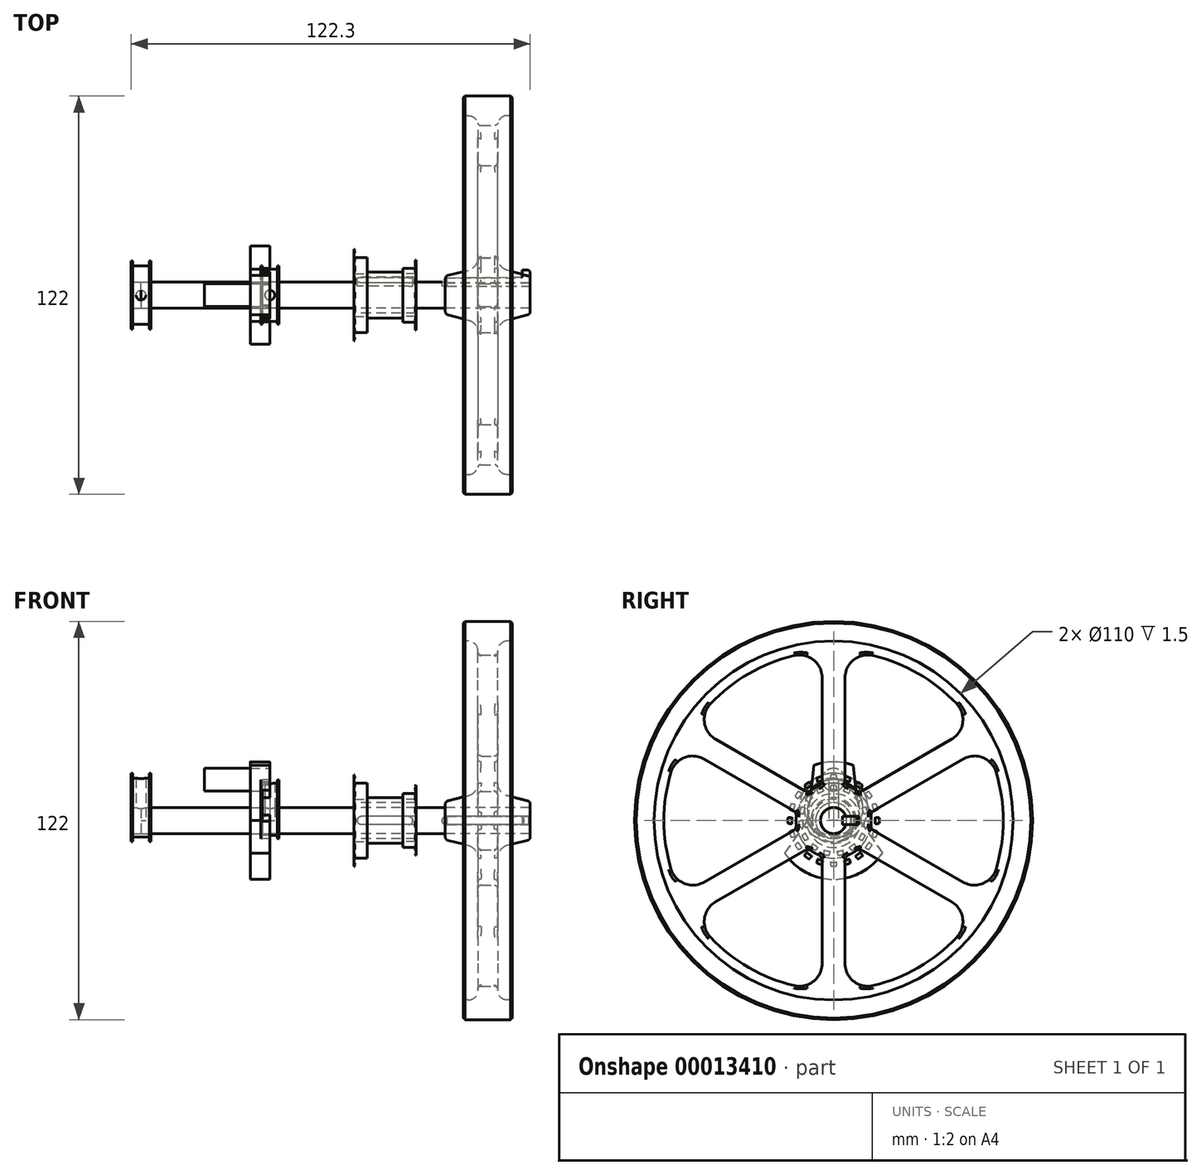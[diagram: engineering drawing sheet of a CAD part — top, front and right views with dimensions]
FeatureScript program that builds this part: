
annotation { "Feature Type Name" : "Feature", "Feature Type Description" : "" }
export const myFeature = defineFeature(function(context is Context, id is Id, definition is map)
    precondition{}
    {
        {
            var Q0;
            Q0=qCreatedBy(makeId("Right.planeOp"),FACE);
            var sketch = newSketch(context, id + "F0", { "sketchPlane" : qUnion([Q0])});
            skCircle(sketch, "E0", {"center": v(0, 0) * mm, "radius": 4 * mm});
            skSolve(sketch);
        }
        {
            var Q0;
            Q0=makeQuery(id+"F0.imprint","IMPRINT",FACE,{"disambiguationData":[TD([[makeQuery(id+"F0.imprint","IMPRINT",EDGE,{"derivedFrom":sQuery(id+"F0.wireOp",EDGE,"E0")}),1.0]])]});
            extrude(context, id + "F1", {"entities" : qUnion([Q0]), "oppositeDirection" : true, "depth" : 39.5 * mm});
        }
        {
            var Q0;
            Q0=makeQuery(id+"F1.opExtrude","CAP_FACE",FACE,{"disambiguationData":[OSD([sQuery(id+"F0.wireOp",EDGE,"E0")])],"isStart":true});
            var sketch = newSketch(context, id + "F2", { "sketchPlane" : qUnion([Q0])});
            skCircle(sketch, "E1", {"center": v(0, 0) * mm, "radius": 18 * mm});
            skLineSegment(sketch, "E2", {"start": v(0, 0) * mm, "end": v(0, 12.5) * mm, "construction": true});
            skCircle(sketch, "E3", {"center": v(0, 12.5) * mm, "radius": 3.5 * mm});
            skLineSegment(sketch, "E4.0", {"start": v(6, 0) * mm, "end": v(6, 16.97) * mm, "construction": true});
            skLineSegment(sketch, "E5", {"start": v(0, 0) * mm, "end": v(8, 0) * mm, "construction": true});
            skLineSegment(sketch, "E6", {"start": v(0, 0) * mm, "end": v(15, 0) * mm, "construction": true});
            skLineSegment(sketch, "E7", {"start": v(15, 0) * mm, "end": v(15, -9.95) * mm, "construction": true});
            skLineSegment(sketch, "E8", {"start": v(6, 16.97) * mm, "end": v(8, 0) * mm});
            skLineSegment(sketch, "E9", {"start": v(8, 0) * mm, "end": v(15, -9.95) * mm});
            skLineSegment(sketch, "E10.0.MirrorCS", {"start": v(-6, 16.97) * mm, "end": v(-8, 0) * mm});
            skLineSegment(sketch, "E11.0.MirrorCS", {"start": v(-8, 0) * mm, "end": v(-15, -9.95) * mm});
            skSolve(sketch);
        }
        {
            var Q0;
            Q0=makeQuery(id+"F2.imprint","IMPRINT",FACE,{"disambiguationData":[TD([[makeQuery(id+"F2.imprint","IMPRINT",EDGE,{"derivedFrom":sQuery(id+"F2.wireOp",EDGE,"E3")}),-1.0]])]});
            extrude(context, id + "F3", {"entities" : qUnion([Q0]), "oppositeDirection" : true, "depth" : 6 * mm});
        }
        {
            var Q0;
            Q0=makeQuery(id+"F2.imprint","IMPRINT",FACE,{"disambiguationData":[TD([[makeQuery(id+"F2.imprint","IMPRINT",EDGE,{"derivedFrom":sQuery(id+"F2.wireOp",EDGE,"E3")}),1.0]])]});
            extrude(context, id + "F4", {"entities" : qUnion([Q0]), "oppositeDirection" : true, "depth" : 20 * mm});
        }
        {
            var Q0;
            Q0=makeQuery(id+"F2.imprint","IMPRINT",FACE,{"disambiguationData":[TD([[makeQuery(id+"F2.imprint","IMPRINT",EDGE,{"derivedFrom":makeQuery(id+"F1.opExtrude","CAP_EDGE",EDGE,{"disambiguationData":[OSD([sQuery(id+"F0.wireOp",EDGE,"E0")])],"isStart":true})}),1.0]])]});
            extrude(context, id + "F5", {"entities" : qUnion([Q0]), "depth" : 79.8 * mm});
        }
        {
            var Q0;
            Q0=qCreatedBy(makeId("Front.planeOp"),FACE);
            cPlane(context, id + "F6", {"entities" : qUnion([Q0]), "cplaneType" : CPlaneType.OFFSET, "offset" : 4 * mm, "oppositeDirection" : true, "width" : 150 * mm, "height" : 150 * mm});
        }
        {
            var Q0;
            Q0=qCreatedBy(id+"F6.planeOp",FACE);
            var sketch = newSketch(context, id + "F7", { "sketchPlane" : qUnion([Q0])});
            skLineSegment(sketch, "E12.0", {"start": v(79.8, 4) * mm, "end": v(79.8, -4) * mm});
            skLineSegment(sketch, "E13", {"start": v(79.8, 0) * mm, "end": v(37.83, 0) * mm, "construction": true});
            skCircle(sketch, "E14", {"center": v(54.05, 0) * mm, "radius": 1.25 * mm});
            skCircle(sketch, "E15", {"center": v(42.55, 0) * mm, "radius": 1.25 * mm});
            skCircle(sketch, "E16", {"center": v(28.05, 0) * mm, "radius": 1.25 * mm});
            skLineSegment(sketch, "E17", {"start": v(54.05, -1.25) * mm, "end": v(79.8, -1.25) * mm});
            skLineSegment(sketch, "E18", {"start": v(42.55, 1.25) * mm, "end": v(28.05, 1.25) * mm});
            skLineSegment(sketch, "E19", {"start": v(42.55, -1.25) * mm, "end": v(28.05, -1.25) * mm});
            skLineSegment(sketch, "E20.0.MirrorCS", {"start": v(54.05, 1.25) * mm, "end": v(79.8, 1.25) * mm});
            skSolve(sketch);
        }
        {
            var Q0;
            {var subQ1=sQuery(id+"F7.wireOp",EDGE,"E17");Q0=makeQuery(id+"F7.imprint","IMPRINT",FACE,{"disambiguationData":[TD([[makeQuery(id+"F7.imprint","IMPRINT",EDGE,{"derivedFrom":subQ1}),1.0]])]});}
            var Q1;
            {var subQ0=sQuery(id+"F7.wireOp",EDGE,"E14");var subQ2=makeQuery(id+"F7.imprint","INTERSECT",VERTEX,{"derivedFrom":[subQ0,sQuery(id+"F7.wireOp",EDGE,"E17")]});Q1=makeQuery(id+"F7.imprint","IMPRINT",FACE,{"disambiguationData":[TD([[makeQuery(id+"F7.imprint","IMPRINT",EDGE,{"disambiguationData":[TD([[subQ2,1.0]])],"derivedFrom":subQ0}),1.0]])]});}
            var Q2;
            {var subQ1=sQuery(id+"F7.wireOp",EDGE,"E18");Q2=makeQuery(id+"F7.imprint","IMPRINT",FACE,{"disambiguationData":[TD([[makeQuery(id+"F7.imprint","IMPRINT",EDGE,{"derivedFrom":subQ1}),1.0]])]});}
            var Q3;
            {var subQ0=sQuery(id+"F7.wireOp",EDGE,"E15");var subQ2=makeQuery(id+"F7.imprint","INTERSECT",VERTEX,{"derivedFrom":[subQ0,sQuery(id+"F7.wireOp",EDGE,"E18")]});Q3=makeQuery(id+"F7.imprint","IMPRINT",FACE,{"disambiguationData":[TD([[makeQuery(id+"F7.imprint","IMPRINT",EDGE,{"disambiguationData":[TD([[subQ2,-1.0]])],"derivedFrom":subQ0}),1.0]])]});}
            var Q4;
            {var subQ0=sQuery(id+"F7.wireOp",EDGE,"E16");var subQ2=makeQuery(id+"F7.imprint","INTERSECT",VERTEX,{"derivedFrom":[subQ0,sQuery(id+"F7.wireOp",EDGE,"E18")]});Q4=makeQuery(id+"F7.imprint","IMPRINT",FACE,{"disambiguationData":[TD([[makeQuery(id+"F7.imprint","IMPRINT",EDGE,{"disambiguationData":[TD([[subQ2,-1.0]])],"derivedFrom":subQ0}),1.0]])]});}
            extrude(context, id + "F8", {"entities" : qUnion([Q0, Q1, Q2, Q3, Q4]), "operationType" : NewBodyOperationType.REMOVE, "depth" : 1.3 * mm});
        }
        {
            var Q0;
            Q0=qCreatedBy(makeId("Front.planeOp"),FACE);
            var sketch = newSketch(context, id + "F9", { "sketchPlane" : qUnion([Q0])});
            skLineSegment(sketch, "E21.0", {"start": v(79.8, 4) * mm, "end": v(79.8, -4) * mm});
            skLineSegment(sketch, "E22.bottom", {"start": v(79.8, 4) * mm, "end": v(53.8, 4) * mm});
            skLineSegment(sketch, "E22.top", {"start": v(79.8, 11.5) * mm, "end": v(53.8, 11.5) * mm});
            skLineSegment(sketch, "E22.left", {"start": v(79.8, 4) * mm, "end": v(79.8, 5.07) * mm});
            skLineSegment(sketch, "E22.right", {"start": v(53.8, 4) * mm, "end": v(53.8, 11.5) * mm});
            skLineSegment(sketch, "E23", {"start": v(66.8, 4) * mm, "end": v(66.8, 61) * mm, "construction": true});
            skLineSegment(sketch, "E24.bottom", {"start": v(74.3, 61) * mm, "end": v(59.3, 61) * mm});
            skLineSegment(sketch, "E24.top", {"start": v(74.3, 55) * mm, "end": v(72.8, 55) * mm});
            skLineSegment(sketch, "E24.left", {"start": v(74.3, 61) * mm, "end": v(74.3, 55) * mm});
            skLineSegment(sketch, "E24.right", {"start": v(59.3, 61) * mm, "end": v(59.3, 55) * mm});
            skLineSegment(sketch, "E25.bottom", {"start": v(60.8, 55) * mm, "end": v(59.3, 55) * mm});
            skLineSegment(sketch, "E25.top", {"start": v(69.8, 11.5) * mm, "end": v(63.8, 11.5) * mm});
            skLineSegment(sketch, "E25.left", {"start": v(69.8, 52) * mm, "end": v(69.8, 11.5) * mm});
            skLineSegment(sketch, "E25.right", {"start": v(63.8, 52) * mm, "end": v(63.8, 11.5) * mm});
            skArc(sketch, "E26.filletArc", {"start": v(72.8, 55) * mm, "mid": v(70.68, 54.12) * mm, "end": v(69.8, 52) * mm});
            skPoint(sketch, "E27.visualSharp", {"position": v(63.8, 55) * mm});
            skArc(sketch, "E27.filletArc", {"start": v(63.8, 52) * mm, "mid": v(62.92, 54.12) * mm, "end": v(60.8, 55) * mm});
            skLineSegment(sketch, "E28", {"start": v(79.05, 6.03) * mm, "end": v(72.81, 7.62) * mm});
            skLineSegment(sketch, "E29", {"start": v(69.8, 11.5) * mm, "end": v(69.8, 11.5) * mm});
            skPoint(sketch, "E30.visualSharp", {"position": v(69.8, 8.4) * mm});
            skArc(sketch, "E30.filletArc", {"start": v(69.8, 11.5) * mm, "mid": v(70.64, 9.05) * mm, "end": v(72.81, 7.62) * mm});
            skPoint(sketch, "E31.newPointB", {"position": v(79.8, 11.5) * mm});
            skArc(sketch, "E31.filletArc", {"start": v(79.8, 5.07) * mm, "mid": v(79.59, 5.68) * mm, "end": v(79.05, 6.03) * mm});
            skArc(sketch, "E32.0.MirrorCS", {"start": v(63.8, 11.5) * mm, "mid": v(62.96, 9.05) * mm, "end": v(60.79, 7.62) * mm});
            skLineSegment(sketch, "E33.0.MirrorCS", {"start": v(54.55, 6.03) * mm, "end": v(60.79, 7.62) * mm});
            skArc(sketch, "E34.0.MirrorCS", {"start": v(53.8, 5.07) * mm, "mid": v(54.01, 5.68) * mm, "end": v(54.55, 6.03) * mm});
            skLineSegment(sketch, "E35", {"start": v(79.8, 0) * mm, "end": v(85.65, 0) * mm, "construction": true});
            skSolve(sketch);
        }
        {
            var Q0;
            Q0=makeQuery(id+"F9.imprint","IMPRINT",FACE,{"disambiguationData":[TD([[makeQuery(id+"F9.imprint","IMPRINT",EDGE,{"derivedFrom":sQuery(id+"F9.wireOp",EDGE,"E24.bottom")}),1.0]])]});
            var Q1;
            {var subQ2=sQuery(id+"F9.wireOp",EDGE,"E22.bottom");Q1=makeQuery(id+"F9.imprint","IMPRINT",FACE,{"disambiguationData":[TD([[makeQuery(id+"F9.imprint","IMPRINT",EDGE,{"derivedFrom":subQ2}),-1.0]])]});}
            var Q2;
            Q2=sQuery(id+"F9.wireOp",EDGE,"E35");
            revolve(context, id + "F10", {"entities" : qUnion([Q0, Q1]), "axis" : qUnion([Q2]), "revolveType" : RevolveType.FULL});
        }
        {
            var Q0;
            Q0=makeQuery(id+"F10.opRevolve","SWEPT_FACE",FACE,{"disambiguationData":[OSD([sQuery(id+"F9.wireOp",EDGE,"E25.left")])]});
            var sketch = newSketch(context, id + "F11", { "sketchPlane" : qUnion([Q0])});
            skLineSegment(sketch, "E36", {"start": v(0, 0) * mm, "end": v(0, 52) * mm, "construction": true});
            skLineSegment(sketch, "E37.0", {"start": v(3.5, 0) * mm, "end": v(3.5, 52) * mm});
            skLineSegment(sketch, "E38.0.MirrorCS", {"start": v(-3.5, 0) * mm, "end": v(-3.5, 52) * mm});
            skLineSegment(sketch, "E39.1.0", {"start": v(-1.75, -3.03) * mm, "end": v(-46.78, 22.97) * mm});
            skLineSegment(sketch, "E39.1.1", {"start": v(1.75, 3.03) * mm, "end": v(-43.28, 29.03) * mm});
            skLineSegment(sketch, "E39.2.0", {"start": v(1.75, -3.03) * mm, "end": v(-43.28, -29.03) * mm});
            skLineSegment(sketch, "E39.2.1", {"start": v(-1.75, 3.03) * mm, "end": v(-46.78, -22.97) * mm});
            skLineSegment(sketch, "E39.3.0", {"start": v(3.5, 0) * mm, "end": v(3.5, -52) * mm});
            skLineSegment(sketch, "E39.3.1", {"start": v(-3.5, 0) * mm, "end": v(-3.5, -52) * mm});
            skLineSegment(sketch, "E39.4.0", {"start": v(1.75, 3.03) * mm, "end": v(46.78, -22.97) * mm});
            skLineSegment(sketch, "E39.4.1", {"start": v(-1.75, -3.03) * mm, "end": v(43.28, -29.03) * mm});
            skLineSegment(sketch, "E39.5.0", {"start": v(-1.75, 3.03) * mm, "end": v(43.28, 29.03) * mm});
            skLineSegment(sketch, "E39.5.1", {"start": v(1.75, -3.03) * mm, "end": v(46.78, 22.97) * mm});
            skPoint(sketch, "E39.center", {"position": v(0, 0) * mm});
            skCircle(sketch, "E40.0", {"center": v(0, 0) * mm, "radius": 52 * mm});
            skSolve(sketch);
        }
        {
            var Q0;
            {var subQ3=sQuery(id+"F11.wireOp",EDGE,"E38.0.MirrorCS");var subQ5=sQuery(id+"F11.wireOp",EDGE,"E40.0");var subQ7=makeQuery(id+"F11.imprint","INTERSECT",VERTEX,{"derivedFrom":[subQ3,subQ5]});Q0=makeQuery(id+"F11.imprint","IMPRINT",FACE,{"disambiguationData":[TD([[makeQuery(id+"F11.imprint","IMPRINT",EDGE,{"disambiguationData":[TD([[subQ7,1.0]])],"derivedFrom":subQ5}),-1.0]])]});}
            var Q1;
            {var subQ3=sQuery(id+"F11.wireOp",EDGE,"E37.0");var subQ5=sQuery(id+"F11.wireOp",EDGE,"E40.0");var subQ7=makeQuery(id+"F11.imprint","INTERSECT",VERTEX,{"derivedFrom":[subQ3,subQ5]});Q1=makeQuery(id+"F11.imprint","IMPRINT",FACE,{"disambiguationData":[TD([[makeQuery(id+"F11.imprint","IMPRINT",EDGE,{"disambiguationData":[TD([[subQ7,-1.0]])],"derivedFrom":subQ5}),-1.0]])]});}
            var Q2;
            {var subQ3=sQuery(id+"F11.wireOp",EDGE,"E39.4.0");var subQ5=sQuery(id+"F11.wireOp",EDGE,"E40.0");var subQ7=makeQuery(id+"F11.imprint","INTERSECT",VERTEX,{"derivedFrom":[subQ3,subQ5]});Q2=makeQuery(id+"F11.imprint","IMPRINT",FACE,{"disambiguationData":[TD([[makeQuery(id+"F11.imprint","IMPRINT",EDGE,{"disambiguationData":[TD([[subQ7,1.0]])],"derivedFrom":subQ5}),-1.0]])]});}
            var Q3;
            {var subQ3=sQuery(id+"F11.wireOp",EDGE,"E39.3.0");var subQ5=sQuery(id+"F11.wireOp",EDGE,"E40.0");var subQ7=makeQuery(id+"F11.imprint","INTERSECT",VERTEX,{"derivedFrom":[subQ3,subQ5]});Q3=makeQuery(id+"F11.imprint","IMPRINT",FACE,{"disambiguationData":[TD([[makeQuery(id+"F11.imprint","IMPRINT",EDGE,{"disambiguationData":[TD([[subQ7,1.0]])],"derivedFrom":subQ5}),-1.0]])]});}
            var Q4;
            {var subQ0=sQuery(id+"F11.wireOp",EDGE,"E40.0");var subQ3=sQuery(id+"F11.wireOp",EDGE,"E39.2.0");var subQ4=makeQuery(id+"F11.imprint","INTERSECT",VERTEX,{"derivedFrom":[subQ3,subQ0]});Q4=makeQuery(id+"F11.imprint","IMPRINT",FACE,{"disambiguationData":[TD([[makeQuery(id+"F11.imprint","IMPRINT",EDGE,{"disambiguationData":[TD([[subQ4,1.0]])],"derivedFrom":subQ0}),-1.0]])]});}
            var Q5;
            {var subQ3=sQuery(id+"F11.wireOp",EDGE,"E39.1.0");var subQ5=sQuery(id+"F11.wireOp",EDGE,"E40.0");var subQ7=makeQuery(id+"F11.imprint","INTERSECT",VERTEX,{"derivedFrom":[subQ3,subQ5]});Q5=makeQuery(id+"F11.imprint","IMPRINT",FACE,{"disambiguationData":[TD([[makeQuery(id+"F11.imprint","IMPRINT",EDGE,{"disambiguationData":[TD([[subQ7,1.0]])],"derivedFrom":subQ5}),-1.0]])]});}
            extrude(context, id + "F12", {"entities" : qUnion([Q0, Q1, Q2, Q3, Q4, Q5]), "operationType" : NewBodyOperationType.REMOVE, "oppositeDirection" : true, "depth" : 6 * mm});
        }
        {
            var Q0;
            Q0=makeQuery(id+"F12.boolean.opBoolean","COPY",EDGE,{"derivedFrom":makeQuery(id+"F12.opExtrude","SWEPT_EDGE",EDGE,{"disambiguationData":[OSD([sQuery(id+"F11.wireOp",EDGE,"E39.2.1"),sQuery(id+"F11.wireOp",EDGE,"E40.0")])]})});
            var Q1;
            Q1=makeQuery(id+"F12.boolean.opBoolean","COPY",EDGE,{"derivedFrom":makeQuery(id+"F12.opExtrude","SWEPT_EDGE",EDGE,{"disambiguationData":[OSD([sQuery(id+"F11.wireOp",EDGE,"E39.2.0"),sQuery(id+"F11.wireOp",EDGE,"E40.0")])]})});
            var Q2;
            Q2=makeQuery(id+"F12.boolean.opBoolean","COPY",EDGE,{"derivedFrom":makeQuery(id+"F12.opExtrude","SWEPT_EDGE",EDGE,{"disambiguationData":[OSD([sQuery(id+"F11.wireOp",EDGE,"E39.3.1"),sQuery(id+"F11.wireOp",EDGE,"E40.0")])]})});
            var Q3;
            Q3=makeQuery(id+"F12.boolean.opBoolean","COPY",EDGE,{"derivedFrom":makeQuery(id+"F12.opExtrude","SWEPT_EDGE",EDGE,{"disambiguationData":[OSD([sQuery(id+"F11.wireOp",EDGE,"E39.4.0"),sQuery(id+"F11.wireOp",EDGE,"E40.0")])]})});
            var Q4;
            Q4=makeQuery(id+"F12.boolean.opBoolean","COPY",EDGE,{"derivedFrom":makeQuery(id+"F12.opExtrude","SWEPT_EDGE",EDGE,{"disambiguationData":[OSD([sQuery(id+"F11.wireOp",EDGE,"E39.3.0"),sQuery(id+"F11.wireOp",EDGE,"E40.0")])]})});
            var Q5;
            Q5=makeQuery(id+"F12.boolean.opBoolean","COPY",EDGE,{"derivedFrom":makeQuery(id+"F12.opExtrude","SWEPT_EDGE",EDGE,{"disambiguationData":[OSD([sQuery(id+"F11.wireOp",EDGE,"E39.4.1"),sQuery(id+"F11.wireOp",EDGE,"E40.0")])]})});
            var Q6;
            Q6=makeQuery(id+"F12.boolean.opBoolean","COPY",EDGE,{"derivedFrom":makeQuery(id+"F12.opExtrude","SWEPT_EDGE",EDGE,{"disambiguationData":[OSD([sQuery(id+"F11.wireOp",EDGE,"E39.5.1"),sQuery(id+"F11.wireOp",EDGE,"E40.0")])]})});
            var Q7;
            Q7=makeQuery(id+"F12.boolean.opBoolean","COPY",EDGE,{"derivedFrom":makeQuery(id+"F12.opExtrude","SWEPT_EDGE",EDGE,{"disambiguationData":[OSD([sQuery(id+"F11.wireOp",EDGE,"E39.5.0"),sQuery(id+"F11.wireOp",EDGE,"E40.0")])]})});
            var Q8;
            Q8=makeQuery(id+"F12.boolean.opBoolean","COPY",EDGE,{"derivedFrom":makeQuery(id+"F12.opExtrude","SWEPT_EDGE",EDGE,{"disambiguationData":[OSD([sQuery(id+"F11.wireOp",EDGE,"E38.0.MirrorCS"),sQuery(id+"F11.wireOp",EDGE,"E40.0")])]})});
            var Q9;
            Q9=makeQuery(id+"F12.boolean.opBoolean","COPY",EDGE,{"derivedFrom":makeQuery(id+"F12.opExtrude","SWEPT_EDGE",EDGE,{"disambiguationData":[OSD([sQuery(id+"F11.wireOp",EDGE,"E37.0"),sQuery(id+"F11.wireOp",EDGE,"E40.0")])]})});
            var Q10;
            Q10=makeQuery(id+"F12.boolean.opBoolean","COPY",EDGE,{"derivedFrom":makeQuery(id+"F12.opExtrude","SWEPT_EDGE",EDGE,{"disambiguationData":[OSD([sQuery(id+"F11.wireOp",EDGE,"E39.1.0"),sQuery(id+"F11.wireOp",EDGE,"E40.0")])]})});
            var Q11;
            Q11=makeQuery(id+"F12.boolean.opBoolean","COPY",EDGE,{"derivedFrom":makeQuery(id+"F12.opExtrude","SWEPT_EDGE",EDGE,{"disambiguationData":[OSD([sQuery(id+"F11.wireOp",EDGE,"E39.1.1"),sQuery(id+"F11.wireOp",EDGE,"E40.0")])]})});
            fillet(context, id + "F13", {"entities" : qUnion([Q0, Q1, Q2, Q3, Q4, Q5, Q6, Q7, Q8, Q9, Q10, Q11]), "radius" : 7 * mm, "tangentPropagation" : true, "allowEdgeOverflow" : false});
        }
        {
            var Q0;
            Q0=makeQuery(id+"F12.boolean.opBoolean","COPY",EDGE,{"derivedFrom":makeQuery(id+"F12.opExtrude","SWEPT_EDGE",EDGE,{"disambiguationData":[OSD([sQuery(id+"F9.wireOp",EDGE,"E25.top"),sQuery(id+"F9.wireOp",EDGE,"E25.left"),sQuery(id+"F9.wireOp",EDGE,"E30.filletArc"),sQuery(id+"F11.wireOp",EDGE,"E39.4.0")])]})});
            var Q1;
            Q1=makeQuery(id+"F12.boolean.opBoolean","COPY",EDGE,{"derivedFrom":makeQuery(id+"F12.opExtrude","SWEPT_EDGE",EDGE,{"disambiguationData":[OSD([sQuery(id+"F9.wireOp",EDGE,"E25.top"),sQuery(id+"F9.wireOp",EDGE,"E25.left"),sQuery(id+"F9.wireOp",EDGE,"E30.filletArc"),sQuery(id+"F11.wireOp",EDGE,"E39.5.1")])]})});
            var Q2;
            Q2=makeQuery(id+"F12.boolean.opBoolean","COPY",EDGE,{"derivedFrom":makeQuery(id+"F12.opExtrude","SWEPT_EDGE",EDGE,{"disambiguationData":[OSD([sQuery(id+"F9.wireOp",EDGE,"E25.top"),sQuery(id+"F9.wireOp",EDGE,"E25.left"),sQuery(id+"F9.wireOp",EDGE,"E30.filletArc"),sQuery(id+"F11.wireOp",EDGE,"E37.0")])]})});
            var Q3;
            Q3=makeQuery(id+"F12.boolean.opBoolean","COPY",EDGE,{"derivedFrom":makeQuery(id+"F12.opExtrude","SWEPT_EDGE",EDGE,{"disambiguationData":[OSD([sQuery(id+"F9.wireOp",EDGE,"E25.top"),sQuery(id+"F9.wireOp",EDGE,"E25.left"),sQuery(id+"F9.wireOp",EDGE,"E30.filletArc"),sQuery(id+"F11.wireOp",EDGE,"E39.5.0")])]})});
            var Q4;
            Q4=makeQuery(id+"F12.boolean.opBoolean","COPY",EDGE,{"derivedFrom":makeQuery(id+"F12.opExtrude","SWEPT_EDGE",EDGE,{"disambiguationData":[OSD([sQuery(id+"F9.wireOp",EDGE,"E25.top"),sQuery(id+"F9.wireOp",EDGE,"E25.left"),sQuery(id+"F9.wireOp",EDGE,"E30.filletArc"),sQuery(id+"F11.wireOp",EDGE,"E38.0.MirrorCS")])]})});
            var Q5;
            Q5=makeQuery(id+"F12.boolean.opBoolean","COPY",EDGE,{"derivedFrom":makeQuery(id+"F12.opExtrude","SWEPT_EDGE",EDGE,{"disambiguationData":[OSD([sQuery(id+"F9.wireOp",EDGE,"E25.top"),sQuery(id+"F9.wireOp",EDGE,"E25.left"),sQuery(id+"F9.wireOp",EDGE,"E30.filletArc"),sQuery(id+"F11.wireOp",EDGE,"E39.1.1")])]})});
            var Q6;
            Q6=makeQuery(id+"F12.boolean.opBoolean","COPY",EDGE,{"derivedFrom":makeQuery(id+"F12.opExtrude","SWEPT_EDGE",EDGE,{"disambiguationData":[OSD([sQuery(id+"F9.wireOp",EDGE,"E25.top"),sQuery(id+"F9.wireOp",EDGE,"E25.left"),sQuery(id+"F9.wireOp",EDGE,"E30.filletArc"),sQuery(id+"F11.wireOp",EDGE,"E39.1.0")])]})});
            var Q7;
            Q7=makeQuery(id+"F12.boolean.opBoolean","COPY",EDGE,{"derivedFrom":makeQuery(id+"F12.opExtrude","SWEPT_EDGE",EDGE,{"disambiguationData":[OSD([sQuery(id+"F9.wireOp",EDGE,"E25.top"),sQuery(id+"F9.wireOp",EDGE,"E25.left"),sQuery(id+"F9.wireOp",EDGE,"E30.filletArc"),sQuery(id+"F11.wireOp",EDGE,"E39.2.1")])]})});
            var Q8;
            Q8=makeQuery(id+"F12.boolean.opBoolean","COPY",EDGE,{"derivedFrom":makeQuery(id+"F12.opExtrude","SWEPT_EDGE",EDGE,{"disambiguationData":[OSD([sQuery(id+"F9.wireOp",EDGE,"E25.top"),sQuery(id+"F9.wireOp",EDGE,"E25.left"),sQuery(id+"F9.wireOp",EDGE,"E30.filletArc"),sQuery(id+"F11.wireOp",EDGE,"E39.2.0")])]})});
            var Q9;
            Q9=makeQuery(id+"F12.boolean.opBoolean","COPY",EDGE,{"derivedFrom":makeQuery(id+"F12.opExtrude","SWEPT_EDGE",EDGE,{"disambiguationData":[OSD([sQuery(id+"F9.wireOp",EDGE,"E25.top"),sQuery(id+"F9.wireOp",EDGE,"E25.left"),sQuery(id+"F9.wireOp",EDGE,"E30.filletArc"),sQuery(id+"F11.wireOp",EDGE,"E39.3.1")])]})});
            var Q10;
            Q10=makeQuery(id+"F12.boolean.opBoolean","COPY",EDGE,{"derivedFrom":makeQuery(id+"F12.opExtrude","SWEPT_EDGE",EDGE,{"disambiguationData":[OSD([sQuery(id+"F9.wireOp",EDGE,"E25.top"),sQuery(id+"F9.wireOp",EDGE,"E25.left"),sQuery(id+"F9.wireOp",EDGE,"E30.filletArc"),sQuery(id+"F11.wireOp",EDGE,"E39.3.0")])]})});
            var Q11;
            Q11=makeQuery(id+"F12.boolean.opBoolean","COPY",EDGE,{"derivedFrom":makeQuery(id+"F12.opExtrude","SWEPT_EDGE",EDGE,{"disambiguationData":[OSD([sQuery(id+"F9.wireOp",EDGE,"E25.top"),sQuery(id+"F9.wireOp",EDGE,"E25.left"),sQuery(id+"F9.wireOp",EDGE,"E30.filletArc"),sQuery(id+"F11.wireOp",EDGE,"E39.4.1")])]})});
            fillet(context, id + "F14", {"entities" : qUnion([Q0, Q1, Q2, Q3, Q4, Q5, Q6, Q7, Q8, Q9, Q10, Q11]), "radius" : 2 * mm, "tangentPropagation" : true, "allowEdgeOverflow" : false});
        }
        {
            var Q0;
            {var subQ0=sQuery(id+"F9.wireOp",EDGE,"E25.top");var subQ1=sQuery(id+"F9.wireOp",EDGE,"E25.left");var subQ2=sQuery(id+"F9.wireOp",EDGE,"E30.filletArc");var subQ3=makeQuery(id+"F10.opRevolve","SWEPT_EDGE",EDGE,{"disambiguationData":[OSD([subQ0,subQ1,subQ2])]});Q0=makeQuery(id+"F12.boolean.opBoolean","MERGE",EDGE,{"derivedFrom":[subQ3,makeQuery(id+"F12.opExtrude","CAP_EDGE",EDGE,{"disambiguationData":[OSD([subQ0,subQ1,subQ2]),TDD([makeQuery(id+"F11.imprint","IMPRINT",EDGE,{"disambiguationData":[TD([[makeQuery(id+"F11.imprint","INTERSECT",VERTEX,{"derivedFrom":[subQ3,sQuery(id+"F11.wireOp",EDGE,"E38.0.MirrorCS")]}),1.0]])],"derivedFrom":subQ3})])],"isStart":true})]});}
            var Q1;
            {var subQ0=sQuery(id+"F9.wireOp",EDGE,"E25.top");var subQ1=sQuery(id+"F9.wireOp",EDGE,"E25.left");var subQ2=sQuery(id+"F9.wireOp",EDGE,"E30.filletArc");var subQ3=makeQuery(id+"F10.opRevolve","SWEPT_EDGE",EDGE,{"disambiguationData":[OSD([subQ0,subQ1,subQ2])]});Q1=makeQuery(id+"F12.boolean.opBoolean","MERGE",EDGE,{"derivedFrom":[subQ3,makeQuery(id+"F12.opExtrude","CAP_EDGE",EDGE,{"disambiguationData":[OSD([subQ0,subQ1,subQ2]),TDD([makeQuery(id+"F11.imprint","IMPRINT",EDGE,{"disambiguationData":[TD([[makeQuery(id+"F11.imprint","INTERSECT",VERTEX,{"derivedFrom":[subQ3,sQuery(id+"F11.wireOp",EDGE,"E37.0")]}),-1.0]])],"derivedFrom":subQ3})])],"isStart":true})]});}
            var Q2;
            {var subQ0=sQuery(id+"F9.wireOp",EDGE,"E25.top");var subQ1=sQuery(id+"F9.wireOp",EDGE,"E25.left");var subQ2=sQuery(id+"F9.wireOp",EDGE,"E30.filletArc");var subQ3=makeQuery(id+"F10.opRevolve","SWEPT_EDGE",EDGE,{"disambiguationData":[OSD([subQ0,subQ1,subQ2])]});Q2=makeQuery(id+"F12.boolean.opBoolean","MERGE",EDGE,{"derivedFrom":[subQ3,makeQuery(id+"F12.opExtrude","CAP_EDGE",EDGE,{"disambiguationData":[OSD([subQ0,subQ1,subQ2]),TDD([makeQuery(id+"F11.imprint","IMPRINT",EDGE,{"disambiguationData":[TD([[makeQuery(id+"F11.imprint","INTERSECT",VERTEX,{"derivedFrom":[subQ3,sQuery(id+"F11.wireOp",EDGE,"E39.4.0")]}),1.0]])],"derivedFrom":subQ3})])],"isStart":true})]});}
            var Q3;
            {var subQ0=sQuery(id+"F9.wireOp",EDGE,"E25.top");var subQ1=sQuery(id+"F9.wireOp",EDGE,"E25.left");var subQ2=sQuery(id+"F9.wireOp",EDGE,"E30.filletArc");var subQ3=makeQuery(id+"F10.opRevolve","SWEPT_EDGE",EDGE,{"disambiguationData":[OSD([subQ0,subQ1,subQ2])]});Q3=makeQuery(id+"F12.boolean.opBoolean","MERGE",EDGE,{"derivedFrom":[subQ3,makeQuery(id+"F12.opExtrude","CAP_EDGE",EDGE,{"disambiguationData":[OSD([subQ0,subQ1,subQ2]),TDD([makeQuery(id+"F11.imprint","IMPRINT",EDGE,{"disambiguationData":[TD([[makeQuery(id+"F11.imprint","INTERSECT",VERTEX,{"derivedFrom":[subQ3,sQuery(id+"F11.wireOp",EDGE,"E39.1.0")]}),1.0]])],"derivedFrom":subQ3})])],"isStart":true})]});}
            var Q4;
            {var subQ0=sQuery(id+"F9.wireOp",EDGE,"E25.top");var subQ1=sQuery(id+"F9.wireOp",EDGE,"E25.left");var subQ2=sQuery(id+"F9.wireOp",EDGE,"E30.filletArc");var subQ3=makeQuery(id+"F10.opRevolve","SWEPT_EDGE",EDGE,{"disambiguationData":[OSD([subQ0,subQ1,subQ2])]});Q4=makeQuery(id+"F12.boolean.opBoolean","MERGE",EDGE,{"derivedFrom":[subQ3,makeQuery(id+"F12.opExtrude","CAP_EDGE",EDGE,{"disambiguationData":[OSD([subQ0,subQ1,subQ2]),TDD([makeQuery(id+"F11.imprint","IMPRINT",EDGE,{"disambiguationData":[TD([[makeQuery(id+"F11.imprint","INTERSECT",VERTEX,{"derivedFrom":[subQ3,sQuery(id+"F11.wireOp",EDGE,"E39.2.0")]}),1.0]])],"derivedFrom":subQ3})])],"isStart":true})]});}
            var Q5;
            {var subQ0=sQuery(id+"F9.wireOp",EDGE,"E25.top");var subQ1=sQuery(id+"F9.wireOp",EDGE,"E25.left");var subQ2=sQuery(id+"F9.wireOp",EDGE,"E30.filletArc");var subQ3=makeQuery(id+"F10.opRevolve","SWEPT_EDGE",EDGE,{"disambiguationData":[OSD([subQ0,subQ1,subQ2])]});Q5=makeQuery(id+"F12.boolean.opBoolean","MERGE",EDGE,{"derivedFrom":[subQ3,makeQuery(id+"F12.opExtrude","CAP_EDGE",EDGE,{"disambiguationData":[OSD([subQ0,subQ1,subQ2]),TDD([makeQuery(id+"F11.imprint","IMPRINT",EDGE,{"disambiguationData":[TD([[makeQuery(id+"F11.imprint","INTERSECT",VERTEX,{"derivedFrom":[subQ3,sQuery(id+"F11.wireOp",EDGE,"E39.3.0")]}),1.0]])],"derivedFrom":subQ3})])],"isStart":true})]});}
            var Q6;
            Q6=makeQuery(id+"F12.boolean.opBoolean","COPY",EDGE,{"derivedFrom":makeQuery(id+"F12.opExtrude","CAP_EDGE",EDGE,{"disambiguationData":[OSD([sQuery(id+"F11.wireOp",EDGE,"E39.1.1")])],"isStart":true})});
            var Q7;
            Q7=makeQuery(id+"F12.boolean.opBoolean","COPY",EDGE,{"derivedFrom":makeQuery(id+"F12.opExtrude","CAP_EDGE",EDGE,{"disambiguationData":[OSD([sQuery(id+"F11.wireOp",EDGE,"E39.1.1")])],"isStart":false})});
            var Q8;
            Q8=makeQuery(id+"F12.boolean.opBoolean","COPY",EDGE,{"derivedFrom":makeQuery(id+"F12.opExtrude","CAP_EDGE",EDGE,{"disambiguationData":[OSD([sQuery(id+"F11.wireOp",EDGE,"E39.2.1")])],"isStart":false})});
            var Q9;
            Q9=makeQuery(id+"F12.boolean.opBoolean","COPY",EDGE,{"derivedFrom":makeQuery(id+"F12.opExtrude","CAP_EDGE",EDGE,{"disambiguationData":[OSD([sQuery(id+"F11.wireOp",EDGE,"E39.2.0")])],"isStart":false})});
            var Q10;
            Q10=makeQuery(id+"F12.boolean.opBoolean","COPY",EDGE,{"derivedFrom":makeQuery(id+"F12.opExtrude","CAP_EDGE",EDGE,{"disambiguationData":[OSD([sQuery(id+"F11.wireOp",EDGE,"E39.5.0")])],"isStart":false})});
            var Q11;
            Q11=makeQuery(id+"F12.boolean.opBoolean","COPY",EDGE,{"derivedFrom":makeQuery(id+"F12.opExtrude","CAP_EDGE",EDGE,{"disambiguationData":[OSD([sQuery(id+"F11.wireOp",EDGE,"E39.4.0")])],"isStart":false})});
            var Q12;
            Q12=makeQuery(id+"F12.boolean.opBoolean","COPY",EDGE,{"derivedFrom":makeQuery(id+"F12.opExtrude","CAP_EDGE",EDGE,{"disambiguationData":[OSD([sQuery(id+"F11.wireOp",EDGE,"E39.3.0")])],"isStart":false})});
            fillet(context, id + "F15", {"entities" : qUnion([Q0, Q1, Q2, Q3, Q4, Q5, Q6, Q7, Q8, Q9, Q10, Q11, Q12]), "radius" : 1 * mm, "tangentPropagation" : true, "allowEdgeOverflow" : false});
        }
        {
            var Q0;
            Q0=makeQuery(id+"F10.opRevolve","SWEPT_EDGE",EDGE,{"disambiguationData":[OSD([sQuery(id+"F9.wireOp",EDGE,"E24.bottom"),sQuery(id+"F9.wireOp",EDGE,"E24.left")])]});
            var Q1;
            Q1=makeQuery(id+"F10.opRevolve","SWEPT_EDGE",EDGE,{"disambiguationData":[OSD([sQuery(id+"F9.wireOp",EDGE,"E24.bottom"),sQuery(id+"F9.wireOp",EDGE,"E24.right")])]});
            chamfer(context, id + "F16", {"entities" : qUnion([Q0, Q1]), "width" : 0.5 * mm, "tangentPropagation" : true});
        }
        {
            var Q0;
            Q0=makeQuery(id+"F10.opRevolve","SWEPT_FACE",FACE,{"disambiguationData":[OSD([sQuery(id+"F9.wireOp",EDGE,"E22.left")])]});
            var sketch = newSketch(context, id + "F17", { "sketchPlane" : qUnion([Q0])});
            skLineSegment(sketch, "E41.0", {"start": v(2.7, 1.25) * mm, "end": v(3.8, 1.25) * mm});
            skLineSegment(sketch, "E41.1", {"start": v(2.7, -1.25) * mm, "end": v(3.8, -1.25) * mm});
            skLineSegment(sketch, "E42", {"start": v(3.8, 1.25) * mm, "end": v(6.32, 1.25) * mm});
            skLineSegment(sketch, "E43", {"start": v(6.32, 1.25) * mm, "end": v(6.32, -1.25) * mm});
            skLineSegment(sketch, "E44", {"start": v(6.32, -1.25) * mm, "end": v(3.8, -1.25) * mm});
            skLineSegment(sketch, "E45", {"start": v(2.7, 1.25) * mm, "end": v(2.7, -1.25) * mm});
            skLineSegment(sketch, "E46", {"start": v(5.3, 1.25) * mm, "end": v(5.3, -1.25) * mm});
            skSolve(sketch);
        }
        {
            var Q0;
            {var subQ0=sQuery(id+"F9.wireOp",EDGE,"E22.left");var subQ4=sQuery(id+"F17.wireOp",EDGE,"E42");var subQ6=makeQuery(id+"F10.opRevolve","SWEPT_EDGE",EDGE,{"disambiguationData":[OSD([subQ0,sQuery(id+"F9.wireOp",EDGE,"E31.filletArc")])]});var subQ8=makeQuery(id+"F17.imprint","INTERSECT",VERTEX,{"derivedFrom":[subQ6,subQ4]});Q0=makeQuery(id+"F17.imprint","IMPRINT",FACE,{"disambiguationData":[TD([[makeQuery(id+"F17.imprint","IMPRINT",EDGE,{"disambiguationData":[TD([[subQ8,1.0]])],"derivedFrom":subQ4}),-1.0]])]});}
            var Q1;
            {var subQ2=sQuery(id+"F17.wireOp",EDGE,"E43");Q1=makeQuery(id+"F17.imprint","IMPRINT",FACE,{"disambiguationData":[TD([[makeQuery(id+"F17.imprint","IMPRINT",EDGE,{"derivedFrom":subQ2}),-1.0]])]});}
            var Q2;
            {var subQ5=sQuery(id+"F17.wireOp",EDGE,"E46");Q2=makeQuery(id+"F17.imprint","IMPRINT",FACE,{"disambiguationData":[TD([[makeQuery(id+"F17.imprint","IMPRINT",EDGE,{"derivedFrom":subQ5}),-1.0]])]});}
            extrude(context, id + "F18", {"entities" : qUnion([Q0, Q1, Q2]), "operationType" : NewBodyOperationType.REMOVE, "oppositeDirection" : true, "depth" : 2.5 * mm});
        }
        {
            var Q0;
            {var subQ0=sQuery(id+"F9.wireOp",EDGE,"E22.left");var subQ4=sQuery(id+"F17.wireOp",EDGE,"E42");var subQ6=makeQuery(id+"F10.opRevolve","SWEPT_EDGE",EDGE,{"disambiguationData":[OSD([subQ0,sQuery(id+"F9.wireOp",EDGE,"E31.filletArc")])]});var subQ8=makeQuery(id+"F17.imprint","INTERSECT",VERTEX,{"derivedFrom":[subQ6,subQ4]});Q0=makeQuery(id+"F17.imprint","IMPRINT",FACE,{"disambiguationData":[TD([[makeQuery(id+"F17.imprint","IMPRINT",EDGE,{"disambiguationData":[TD([[subQ8,1.0]])],"derivedFrom":subQ4}),-1.0]])]});}
            var Q1;
            {var subQ5=sQuery(id+"F17.wireOp",EDGE,"E46");Q1=makeQuery(id+"F17.imprint","IMPRINT",FACE,{"disambiguationData":[TD([[makeQuery(id+"F17.imprint","IMPRINT",EDGE,{"derivedFrom":subQ5}),-1.0]])]});}
            extrude(context, id + "F19", {"entities" : qUnion([Q0, Q1]), "operationType" : NewBodyOperationType.REMOVE, "oppositeDirection" : true, "depth" : 26 * mm});
        }
        {
            var Q0;
            Q0=makeQuery(id+"F8.boolean.opBoolean","COPY",FACE,{"derivedFrom":makeQuery(id+"F8.opExtrude","SWEPT_FACE",FACE,{"disambiguationData":[OSD([sQuery(id+"F7.wireOp",EDGE,"E17")])]})});
            var sketch = newSketch(context, id + "F20", { "sketchPlane" : qUnion([Q0])});
            skLineSegment(sketch, "E47", {"start": v(79.8, 2.7) * mm, "end": v(79.8, 7.7) * mm});
            skLineSegment(sketch, "E48", {"start": v(79.8, 7.7) * mm, "end": v(77.3, 7.7) * mm});
            skLineSegment(sketch, "E49", {"start": v(77.3, 7.7) * mm, "end": v(77.3, 5.4) * mm});
            skLineSegment(sketch, "E50", {"start": v(77.3, 5.4) * mm, "end": v(54.3, 5.2) * mm});
            skLineSegment(sketch, "E51", {"start": v(54.3, 5.2) * mm, "end": v(54.3, 2.7) * mm});
            skLineSegment(sketch, "E52", {"start": v(54.3, 2.7) * mm, "end": v(79.8, 2.7) * mm});
            skSolve(sketch);
        }
        {
            var Q0;
            {var subQ6=sQuery(id+"F20.wireOp",EDGE,"E48");Q0=makeQuery(id+"F20.imprint","IMPRINT",FACE,{"disambiguationData":[TD([[makeQuery(id+"F20.imprint","IMPRINT",EDGE,{"derivedFrom":subQ6}),1.0]])]});}
            var Q1;
            {var subQ6=sQuery(id+"F20.wireOp",EDGE,"E52");Q1=makeQuery(id+"F20.imprint","IMPRINT",FACE,{"disambiguationData":[TD([[makeQuery(id+"F20.imprint","IMPRINT",EDGE,{"derivedFrom":subQ6}),1.0]])]});}
            extrude(context, id + "F21", {"entities" : qUnion([Q0, Q1]), "depth" : 2.5 * mm});
        }
        {
            var Q0;
            Q0=makeQuery(id+"F21.opExtrude","SWEPT_EDGE",EDGE,{"disambiguationData":[OSD([sQuery(id+"F20.wireOp",EDGE,"E47"),sQuery(id+"F20.wireOp",EDGE,"E48")])]});
            chamfer(context, id + "F22", {"entities" : qUnion([Q0]), "width" : 0.5 * mm, "tangentPropagation" : true});
        }
        {
            var Q0;
            {var subQ1=sQuery(id+"F7.wireOp",EDGE,"E18");Q0=makeQuery(id+"F7.imprint","IMPRINT",FACE,{"disambiguationData":[TD([[makeQuery(id+"F7.imprint","IMPRINT",EDGE,{"derivedFrom":subQ1}),1.0]])]});}
            var Q1;
            {var subQ0=sQuery(id+"F7.wireOp",EDGE,"E15");var subQ2=makeQuery(id+"F7.imprint","INTERSECT",VERTEX,{"derivedFrom":[subQ0,sQuery(id+"F7.wireOp",EDGE,"E18")]});Q1=makeQuery(id+"F7.imprint","IMPRINT",FACE,{"disambiguationData":[TD([[makeQuery(id+"F7.imprint","IMPRINT",EDGE,{"disambiguationData":[TD([[subQ2,-1.0]])],"derivedFrom":subQ0}),1.0]])]});}
            var Q2;
            {var subQ0=sQuery(id+"F7.wireOp",EDGE,"E16");var subQ2=makeQuery(id+"F7.imprint","INTERSECT",VERTEX,{"derivedFrom":[subQ0,sQuery(id+"F7.wireOp",EDGE,"E18")]});Q2=makeQuery(id+"F7.imprint","IMPRINT",FACE,{"disambiguationData":[TD([[makeQuery(id+"F7.imprint","IMPRINT",EDGE,{"disambiguationData":[TD([[subQ2,-1.0]])],"derivedFrom":subQ0}),1.0]])]});}
            extrude(context, id + "F23", {"entities" : qUnion([Q0, Q1, Q2]), "endBound" : BoundingType.SYMMETRIC, "depth" : 2.5 * mm});
        }
        {
            var Q0;
            Q0=makeQuery(id+"F5.opExtrude","CAP_FACE",FACE,{"disambiguationData":[OSD([sQuery(id+"F0.wireOp",EDGE,"E0")])],"isStart":false});
            cPlane(context, id + "F24", {"entities" : qUnion([Q0]), "cplaneType" : CPlaneType.OFFSET, "offset" : (27 + 9 + 8.5) * mm, "oppositeDirection" : true, "width" : 150 * mm, "height" : 150 * mm});
        }
        {
            var Q0;
            Q0=qCreatedBy(id+"F24.planeOp",FACE);
            var sketch = newSketch(context, id + "F25", { "sketchPlane" : qUnion([Q0])});
            skCircle(sketch, "E53", {"center": v(0, 0) * mm, "radius": 5.5 * mm});
            skLineSegment(sketch, "E54.0", {"start": v(2.75, 1.25) * mm, "end": v(5.36, 1.25) * mm});
            skLineSegment(sketch, "E54.1", {"start": v(2.75, -1.25) * mm, "end": v(5.36, -1.25) * mm});
            skPoint(sketch, "E55.orphan", {"position": v(5.25, 1.25) * mm});
            skPoint(sketch, "E56.orphan", {"position": v(5.25, -1.25) * mm});
            skCircle(sketch, "E57.0", {"center": v(0, 0) * mm, "radius": 4 * mm});
            skSolve(sketch);
        }
        {
            var Q0;
            {var subQ3=sQuery(id+"F25.wireOp",EDGE,"E54.0");var subQ5=sQuery(id+"F25.wireOp",EDGE,"E53");var subQ7=makeQuery(id+"F25.imprint","INTERSECT",VERTEX,{"derivedFrom":[subQ5,subQ3]});Q0=makeQuery(id+"F25.imprint","IMPRINT",FACE,{"disambiguationData":[TD([[makeQuery(id+"F25.imprint","IMPRINT",EDGE,{"disambiguationData":[TD([[subQ7,-1.0]])],"derivedFrom":subQ5}),1.0]])]});}
            extrude(context, id + "F26", {"entities" : qUnion([Q0]), "endBound" : BoundingType.SYMMETRIC, "depth" : 19 * mm});
        }
        {
            var Q0;
            Q0=qCreatedBy(id+"F24.planeOp",FACE);
            var sketch = newSketch(context, id + "F27", { "sketchPlane" : qUnion([Q0])});
            skArc(sketch, "E58.0", {"start": v(5.36, 1.25) * mm, "mid": v(-5.5, 0) * mm, "end": v(5.36, -1.25) * mm});
            skCircle(sketch, "E59", {"center": v(0, 0) * mm, "radius": 6.5 * mm});
            skCircle(sketch, "E60", {"center": v(0, 0) * mm, "radius": 7 * mm});
            skCircle(sketch, "E61.0", {"center": v(0, 0) * mm, "radius": 4 * mm});
            skCircle(sketch, "E62", {"center": v(0, 0) * mm, "radius": 5.5 * mm});
            skSolve(sketch);
        }
        {
            var Q0;
            Q0=makeQuery(id+"F27.imprint","IMPRINT",FACE,{"disambiguationData":[TD([[makeQuery(id+"F27.imprint","IMPRINT",EDGE,{"derivedFrom":sQuery(id+"F27.wireOp",EDGE,"E59")}),1.0]])]});
            extrude(context, id + "F28", {"entities" : qUnion([Q0]), "endBound" : BoundingType.SYMMETRIC, "depth" : 19 * mm});
        }
        {
            var Q0;
            Q0=makeQuery(id+"F27.imprint","IMPRINT",FACE,{"disambiguationData":[TD([[makeQuery(id+"F27.imprint","IMPRINT",EDGE,{"derivedFrom":sQuery(id+"F27.wireOp",EDGE,"E59")}),-1.0]])]});
            extrude(context, id + "F29", {"entities" : qUnion([Q0]), "operationType" : NewBodyOperationType.ADD, "endBound" : BoundingType.SYMMETRIC, "depth" : 11 * mm});
        }
        {
            var Q0;
            Q0=makeQuery(id+"F5.opExtrude","CAP_FACE",FACE,{"disambiguationData":[OSD([sQuery(id+"F0.wireOp",EDGE,"E0")])],"isStart":true});
            var sketch = newSketch(context, id + "F30", { "sketchPlane" : qUnion([Q0])});
            skLineSegment(sketch, "E63", {"start": v(0, 0) * mm, "end": v(0, 3.5) * mm, "construction": true});
            skCircle(sketch, "E64", {"center": v(0, 3.5) * mm, "radius": 9 * mm});
            skCircle(sketch, "E65", {"center": v(0, 3.5) * mm, "radius": 8 * mm});
            skSolve(sketch);
        }
        {
            var Q0;
            Q0=makeQuery(id+"F30.imprint","IMPRINT",FACE,{"disambiguationData":[TD([[makeQuery(id+"F30.imprint","IMPRINT",EDGE,{"derivedFrom":sQuery(id+"F30.wireOp",EDGE,"E65")}),1.0]])]});
            var Q1;
            Q1=makeQuery(id+"F30.imprint","IMPRINT",FACE,{"disambiguationData":[TD([[makeQuery(id+"F30.imprint","IMPRINT",EDGE,{"derivedFrom":sQuery(id+"F30.wireOp",EDGE,"E64")}),1.0]])]});
            extrude(context, id + "F31", {"entities" : qUnion([Q0, Q1]), "endBound" : BoundingType.SYMMETRIC, "depth" : 5.5 * mm});
        }
        {
            var Q0;
            Q0=makeQuery(id+"F30.imprint","IMPRINT",FACE,{"disambiguationData":[TD([[makeQuery(id+"F30.imprint","IMPRINT",EDGE,{"derivedFrom":sQuery(id+"F30.wireOp",EDGE,"E64")}),1.0]])]});
            extrude(context, id + "F32", {"entities" : qUnion([Q0]), "operationType" : NewBodyOperationType.REMOVE, "endBound" : BoundingType.SYMMETRIC, "oppositeDirection" : true, "depth" : 4.5 * mm});
        }
        {
            var Q0;
            Q0=qCreatedBy(makeId("Top.planeOp"),FACE);
            var sketch = newSketch(context, id + "F33", { "sketchPlane" : qUnion([Q0])});
            skCircle(sketch, "E66", {"center": v(0, 0) * mm, "radius": 1.5 * mm});
            skSolve(sketch);
        }
        {
            var Q0;
            Q0=makeQuery(id+"F33.imprint","IMPRINT",FACE,{"disambiguationData":[TD([[makeQuery(id+"F33.imprint","IMPRINT",EDGE,{"derivedFrom":sQuery(id+"F33.wireOp",EDGE,"E66")}),1.0]])]});
            extrude(context, id + "F34", {"entities" : qUnion([Q0]), "operationType" : NewBodyOperationType.REMOVE, "depth" : 11.5 * mm});
        }
        {
            var Q0;
            Q0=makeQuery(id+"F1.opExtrude","CAP_FACE",FACE,{"disambiguationData":[OSD([sQuery(id+"F0.wireOp",EDGE,"E0")])],"isStart":false});
            var sketch = newSketch(context, id + "F35", { "sketchPlane" : qUnion([Q0])});
            skLineSegment(sketch, "E67", {"start": v(0, 0) * mm, "end": v(0, 4) * mm, "construction": true});
            skCircle(sketch, "E68", {"center": v(0, 4) * mm, "radius": 9 * mm});
            skCircle(sketch, "E69", {"center": v(0, 4) * mm, "radius": 10.5 * mm});
            skSolve(sketch);
        }
        {
            var Q0;
            Q0=makeQuery(id+"F35.imprint","IMPRINT",FACE,{"disambiguationData":[TD([[makeQuery(id+"F35.imprint","IMPRINT",EDGE,{"derivedFrom":sQuery(id+"F35.wireOp",EDGE,"E68")}),1.0]])]});
            var Q1;
            Q1=makeQuery(id+"F35.imprint","IMPRINT",FACE,{"disambiguationData":[TD([[makeQuery(id+"F35.imprint","IMPRINT",EDGE,{"derivedFrom":sQuery(id+"F35.wireOp",EDGE,"E68")}),-1.0]])]});
            extrude(context, id + "F36", {"entities" : qUnion([Q0, Q1]), "endBound" : BoundingType.SYMMETRIC, "depth" : 6 * mm});
        }
        {
            var Q0;
            Q0=makeQuery(id+"F35.imprint","IMPRINT",FACE,{"disambiguationData":[TD([[makeQuery(id+"F35.imprint","IMPRINT",EDGE,{"derivedFrom":sQuery(id+"F35.wireOp",EDGE,"E68")}),-1.0]])]});
            extrude(context, id + "F37", {"entities" : qUnion([Q0]), "operationType" : NewBodyOperationType.REMOVE, "endBound" : BoundingType.SYMMETRIC, "oppositeDirection" : true, "depth" : 5 * mm});
        }
        {
            var Q0;
            Q0=qCreatedBy(makeId("Top.planeOp"),FACE);
            var sketch = newSketch(context, id + "F38", { "sketchPlane" : qUnion([Q0])});
            skLineSegment(sketch, "E70.0", {"start": v(-42.5, 4) * mm, "end": v(-42.5, -4) * mm});
            skLineSegment(sketch, "E70.1", {"start": v(-36.5, 4) * mm, "end": v(-36.5, -4) * mm});
            skLineSegment(sketch, "E71", {"start": v(-42.5, 0) * mm, "end": v(-36.5, 0) * mm, "construction": true});
            skCircle(sketch, "E72", {"center": v(-39.5, 0) * mm, "radius": 1.5 * mm});
            skSolve(sketch);
        }
        {
            var Q0;
            Q0=makeQuery(id+"F38.imprint","IMPRINT",FACE,{"disambiguationData":[TD([[makeQuery(id+"F38.imprint","IMPRINT",EDGE,{"derivedFrom":sQuery(id+"F38.wireOp",EDGE,"E72")}),1.0]])]});
            extrude(context, id + "F39", {"entities" : qUnion([Q0]), "operationType" : NewBodyOperationType.REMOVE, "depth" : 13 * mm});
        }
        {
            var Q0;
            Q0=makeQuery(id+"F29.opExtrude","CAP_FACE",FACE,{"disambiguationData":[OSD([sQuery(id+"F27.wireOp",EDGE,"E59"),sQuery(id+"F27.wireOp",EDGE,"E60")])],"isStart":false});
            var sketch = newSketch(context, id + "F40", { "sketchPlane" : qUnion([Q0])});
            skCircle(sketch, "E73", {"center": v(0, 0) * mm, "radius": 8.25 * mm});
            skCircle(sketch, "E74", {"center": v(0, 0) * mm, "radius": 10.75 * mm});
            skCircle(sketch, "E75", {"center": v(0, 0) * mm, "radius": 9.5 * mm, "construction": true});
            skLineSegment(sketch, "E76", {"start": v(0, 0) * mm, "end": v(0, 10.75) * mm, "construction": true});
            skLineSegment(sketch, "E77", {"start": v(0, 0) * mm, "end": v(-1, 9.45) * mm, "construction": true});
            skLineSegment(sketch, "E78", {"start": v(0, 8.25) * mm, "end": v(15, 8.25) * mm, "construction": true});
            skArc(sketch, "E79", {"start": v(-0.85, 10.72) * mm, "mid": v(-1, 9.45) * mm, "end": v(-1.04, 8.18) * mm});
            skArc(sketch, "E80.0.MirrorCS", {"start": v(0.85, 10.72) * mm, "mid": v(1, 9.45) * mm, "end": v(1.04, 8.18) * mm});
            skArc(sketch, "E81.1.0", {"start": v(-5.13, 9.45) * mm, "mid": v(-4.75, 8.23) * mm, "end": v(-4.28, 7.05) * mm});
            skArc(sketch, "E81.1.1", {"start": v(-3.59, 10.13) * mm, "mid": v(-2.94, 9.04) * mm, "end": v(-2.38, 7.9) * mm});
            skArc(sketch, "E81.2.0", {"start": v(-8.53, 6.54) * mm, "mid": v(-7.7, 5.59) * mm, "end": v(-6.78, 4.7) * mm});
            skArc(sketch, "E81.2.1", {"start": v(-7.4, 7.8) * mm, "mid": v(-6.36, 7.06) * mm, "end": v(-5.39, 6.25) * mm});
            skArc(sketch, "E81.3.0", {"start": v(-10.45, 2.5) * mm, "mid": v(-9.3, 1.98) * mm, "end": v(-8.1, 1.54) * mm});
            skArc(sketch, "E81.3.1", {"start": v(-9.93, 4.12) * mm, "mid": v(-8.68, 3.87) * mm, "end": v(-7.46, 3.52) * mm});
            skArc(sketch, "E81.4.0", {"start": v(-10.57, -1.96) * mm, "mid": v(-9.3, -1.98) * mm, "end": v(-8.03, -1.89) * mm});
            skArc(sketch, "E81.4.1", {"start": v(-10.75, -0.28) * mm, "mid": v(-9.5, 0) * mm, "end": v(-8.25, 0.18) * mm});
            skArc(sketch, "E81.5.0", {"start": v(-8.86, -6.1) * mm, "mid": v(-7.7, -5.59) * mm, "end": v(-6.57, -5) * mm});
            skArc(sketch, "E81.5.1", {"start": v(-9.7, -4.62) * mm, "mid": v(-8.68, -3.87) * mm, "end": v(-7.6, -3.2) * mm});
            skArc(sketch, "E81.6.0", {"start": v(-5.61, -9.17) * mm, "mid": v(-4.75, -8.23) * mm, "end": v(-3.97, -7.23) * mm});
            skArc(sketch, "E81.6.1", {"start": v(-6.98, -8.17) * mm, "mid": v(-6.36, -7.07) * mm, "end": v(-5.65, -6.01) * mm});
            skArc(sketch, "E81.7.0", {"start": v(-1.4, -10.66) * mm, "mid": v(-1, -9.45) * mm, "end": v(-0.69, -8.22) * mm});
            skArc(sketch, "E81.7.1", {"start": v(-3.06, -10.3) * mm, "mid": v(-2.94, -9.04) * mm, "end": v(-2.72, -7.79) * mm});
            skArc(sketch, "E81.8.0", {"start": v(3.06, -10.3) * mm, "mid": v(2.94, -9.04) * mm, "end": v(2.72, -7.79) * mm});
            skArc(sketch, "E81.8.1", {"start": v(1.4, -10.66) * mm, "mid": v(1, -9.45) * mm, "end": v(0.69, -8.22) * mm});
            skArc(sketch, "E81.9.0", {"start": v(6.98, -8.17) * mm, "mid": v(6.36, -7.07) * mm, "end": v(5.65, -6.01) * mm});
            skArc(sketch, "E81.9.1", {"start": v(5.61, -9.17) * mm, "mid": v(4.75, -8.23) * mm, "end": v(3.97, -7.23) * mm});
            skArc(sketch, "E81.10.0", {"start": v(9.7, -4.62) * mm, "mid": v(8.68, -3.87) * mm, "end": v(7.6, -3.2) * mm});
            skArc(sketch, "E81.10.1", {"start": v(8.86, -6.1) * mm, "mid": v(7.7, -5.59) * mm, "end": v(6.57, -5) * mm});
            skArc(sketch, "E81.11.0", {"start": v(10.75, -0.28) * mm, "mid": v(9.5, 0) * mm, "end": v(8.25, 0.18) * mm});
            skArc(sketch, "E81.11.1", {"start": v(10.57, -1.96) * mm, "mid": v(9.3, -1.98) * mm, "end": v(8.03, -1.89) * mm});
            skArc(sketch, "E81.12.0", {"start": v(9.93, 4.12) * mm, "mid": v(8.68, 3.87) * mm, "end": v(7.46, 3.52) * mm});
            skArc(sketch, "E81.12.1", {"start": v(10.45, 2.5) * mm, "mid": v(9.3, 1.98) * mm, "end": v(8.1, 1.54) * mm});
            skArc(sketch, "E81.13.0", {"start": v(7.4, 7.8) * mm, "mid": v(6.36, 7.06) * mm, "end": v(5.39, 6.25) * mm});
            skArc(sketch, "E81.13.1", {"start": v(8.53, 6.54) * mm, "mid": v(7.7, 5.59) * mm, "end": v(6.78, 4.7) * mm});
            skArc(sketch, "E81.14.0", {"start": v(3.59, 10.13) * mm, "mid": v(2.94, 9.04) * mm, "end": v(2.38, 7.9) * mm});
            skArc(sketch, "E81.14.1", {"start": v(5.13, 9.45) * mm, "mid": v(4.75, 8.23) * mm, "end": v(4.28, 7.05) * mm});
            skSolve(sketch);
        }
        {
            var Q0;
            Q0=makeQuery(id+"F40.imprint","IMPRINT",FACE,{"disambiguationData":[TD([[makeQuery(id+"F40.imprint","IMPRINT",EDGE,{"derivedFrom":makeQuery(id+"F29.opExtrude","CAP_EDGE",EDGE,{"disambiguationData":[OSD([sQuery(id+"F27.wireOp",EDGE,"E60")])],"isStart":false})}),-1.0]])]});
            var Q1;
            Q1=makeQuery(id+"F40.imprint","IMPRINT",FACE,{"disambiguationData":[TD([[makeQuery(id+"F40.imprint","IMPRINT",EDGE,{"derivedFrom":makeQuery(id+"F29.opExtrude","CAP_EDGE",EDGE,{"disambiguationData":[OSD([sQuery(id+"F27.wireOp",EDGE,"E60")])],"isStart":false})}),1.0]])]});
            var Q2;
            {var subQ1=sQuery(id+"F40.wireOp",EDGE,"E81.1.0");Q2=makeQuery(id+"F40.imprint","IMPRINT",FACE,{"disambiguationData":[TD([[makeQuery(id+"F40.imprint","IMPRINT",EDGE,{"derivedFrom":subQ1}),1.0]])]});}
            var Q3;
            {var subQ1=sQuery(id+"F40.wireOp",EDGE,"E79");Q3=makeQuery(id+"F40.imprint","IMPRINT",FACE,{"disambiguationData":[TD([[makeQuery(id+"F40.imprint","IMPRINT",EDGE,{"derivedFrom":subQ1}),1.0]])]});}
            var Q4;
            {var subQ1=sQuery(id+"F40.wireOp",EDGE,"E81.14.0");Q4=makeQuery(id+"F40.imprint","IMPRINT",FACE,{"disambiguationData":[TD([[makeQuery(id+"F40.imprint","IMPRINT",EDGE,{"derivedFrom":subQ1}),1.0]])]});}
            var Q5;
            {var subQ1=sQuery(id+"F40.wireOp",EDGE,"E81.13.0");Q5=makeQuery(id+"F40.imprint","IMPRINT",FACE,{"disambiguationData":[TD([[makeQuery(id+"F40.imprint","IMPRINT",EDGE,{"derivedFrom":subQ1}),1.0]])]});}
            var Q6;
            {var subQ1=sQuery(id+"F40.wireOp",EDGE,"E81.12.0");Q6=makeQuery(id+"F40.imprint","IMPRINT",FACE,{"disambiguationData":[TD([[makeQuery(id+"F40.imprint","IMPRINT",EDGE,{"derivedFrom":subQ1}),1.0]])]});}
            var Q7;
            {var subQ1=sQuery(id+"F40.wireOp",EDGE,"E81.11.0");Q7=makeQuery(id+"F40.imprint","IMPRINT",FACE,{"disambiguationData":[TD([[makeQuery(id+"F40.imprint","IMPRINT",EDGE,{"derivedFrom":subQ1}),1.0]])]});}
            var Q8;
            {var subQ1=sQuery(id+"F40.wireOp",EDGE,"E81.10.0");Q8=makeQuery(id+"F40.imprint","IMPRINT",FACE,{"disambiguationData":[TD([[makeQuery(id+"F40.imprint","IMPRINT",EDGE,{"derivedFrom":subQ1}),1.0]])]});}
            var Q9;
            {var subQ1=sQuery(id+"F40.wireOp",EDGE,"E81.9.0");Q9=makeQuery(id+"F40.imprint","IMPRINT",FACE,{"disambiguationData":[TD([[makeQuery(id+"F40.imprint","IMPRINT",EDGE,{"derivedFrom":subQ1}),1.0]])]});}
            var Q10;
            {var subQ1=sQuery(id+"F40.wireOp",EDGE,"E81.8.0");Q10=makeQuery(id+"F40.imprint","IMPRINT",FACE,{"disambiguationData":[TD([[makeQuery(id+"F40.imprint","IMPRINT",EDGE,{"derivedFrom":subQ1}),1.0]])]});}
            var Q11;
            {var subQ1=sQuery(id+"F40.wireOp",EDGE,"E81.7.0");Q11=makeQuery(id+"F40.imprint","IMPRINT",FACE,{"disambiguationData":[TD([[makeQuery(id+"F40.imprint","IMPRINT",EDGE,{"derivedFrom":subQ1}),1.0]])]});}
            var Q12;
            {var subQ1=sQuery(id+"F40.wireOp",EDGE,"E81.6.0");Q12=makeQuery(id+"F40.imprint","IMPRINT",FACE,{"disambiguationData":[TD([[makeQuery(id+"F40.imprint","IMPRINT",EDGE,{"derivedFrom":subQ1}),1.0]])]});}
            var Q13;
            {var subQ1=sQuery(id+"F40.wireOp",EDGE,"E81.5.0");Q13=makeQuery(id+"F40.imprint","IMPRINT",FACE,{"disambiguationData":[TD([[makeQuery(id+"F40.imprint","IMPRINT",EDGE,{"derivedFrom":subQ1}),1.0]])]});}
            var Q14;
            {var subQ1=sQuery(id+"F40.wireOp",EDGE,"E81.4.0");Q14=makeQuery(id+"F40.imprint","IMPRINT",FACE,{"disambiguationData":[TD([[makeQuery(id+"F40.imprint","IMPRINT",EDGE,{"derivedFrom":subQ1}),1.0]])]});}
            var Q15;
            {var subQ1=sQuery(id+"F40.wireOp",EDGE,"E81.3.0");Q15=makeQuery(id+"F40.imprint","IMPRINT",FACE,{"disambiguationData":[TD([[makeQuery(id+"F40.imprint","IMPRINT",EDGE,{"derivedFrom":subQ1}),1.0]])]});}
            var Q16;
            {var subQ1=sQuery(id+"F40.wireOp",EDGE,"E81.2.0");Q16=makeQuery(id+"F40.imprint","IMPRINT",FACE,{"disambiguationData":[TD([[makeQuery(id+"F40.imprint","IMPRINT",EDGE,{"derivedFrom":subQ1}),1.0]])]});}
            extrude(context, id + "F41", {"entities" : qUnion([Q0, Q1, Q2, Q3, Q4, Q5, Q6, Q7, Q8, Q9, Q10, Q11, Q12, Q13, Q14, Q15, Q16]), "depth" : 4 * mm});
        }
        {
            var Q0;
            Q0=qCreatedBy(makeId("Front.planeOp"),FACE);
            var sketch = newSketch(context, id + "F42", { "sketchPlane" : qUnion([Q0])});
            skLineSegment(sketch, "E82.0", {"start": v(40.8, 8.25) * mm, "end": v(40.8, -8.25) * mm});
            skLineSegment(sketch, "E82.1", {"start": v(40.8, 9.5) * mm, "end": v(40.8, -9.5) * mm});
            skLineSegment(sketch, "E82.2", {"start": v(40.8, 10.75) * mm, "end": v(40.8, -10.75) * mm});
            skLineSegment(sketch, "E83.bottom", {"start": v(40.8, 8.25) * mm, "end": v(44.8, 8.25) * mm});
            skLineSegment(sketch, "E83.top", {"start": v(40.8, 10.75) * mm, "end": v(44.8, 10.75) * mm});
            skLineSegment(sketch, "E83.left", {"start": v(40.8, 8.25) * mm, "end": v(40.8, 10.75) * mm});
            skLineSegment(sketch, "E83.right", {"start": v(44.8, 8.25) * mm, "end": v(44.8, 10.75) * mm});
            skLineSegment(sketch, "E84", {"start": v(42.8, 10.75) * mm, "end": v(42.8, 8.25) * mm, "construction": true});
            skLineSegment(sketch, "E85", {"start": v(40.8, 8.25) * mm, "end": v(50.8, 8.25) * mm, "construction": true});
            skLineSegment(sketch, "E86", {"start": v(40.8, 0) * mm, "end": v(46.26, 0) * mm, "construction": true});
            skArc(sketch, "E87", {"start": v(41.04, 10.75) * mm, "mid": v(40.9, 10.13) * mm, "end": v(40.8, 9.5) * mm});
            skArc(sketch, "E88.0.MirrorCS", {"start": v(44.56, 10.75) * mm, "mid": v(44.7, 10.13) * mm, "end": v(44.8, 9.5) * mm});
            skSolve(sketch);
        }
        {
            var Q0;
            {var subQ0=sQuery(id+"F42.wireOp",EDGE,"E87");Q0=makeQuery(id+"F42.imprint","IMPRINT",FACE,{"disambiguationData":[TD([[makeQuery(id+"F42.imprint","IMPRINT",EDGE,{"derivedFrom":subQ0}),-1.0]])]});}
            var Q1;
            {var subQ0=sQuery(id+"F42.wireOp",EDGE,"E88.0.MirrorCS");Q1=makeQuery(id+"F42.imprint","IMPRINT",FACE,{"disambiguationData":[TD([[makeQuery(id+"F42.imprint","IMPRINT",EDGE,{"derivedFrom":subQ0}),1.0]])]});}
            var Q2;
            Q2=sQuery(id+"F42.wireOp",EDGE,"E86");
            revolve(context, id + "F43", {"operationType" : NewBodyOperationType.REMOVE, "entities" : qUnion([Q0, Q1]), "axis" : qUnion([Q2]), "revolveType" : RevolveType.FULL, "oppositeDirection" : true});
        }
        {
            var Q0;
            Q0=makeQuery(id+"F29.opExtrude","CAP_FACE",FACE,{"disambiguationData":[OSD([sQuery(id+"F27.wireOp",EDGE,"E59"),sQuery(id+"F27.wireOp",EDGE,"E60")])],"isStart":true});
            var sketch = newSketch(context, id + "F44", { "sketchPlane" : qUnion([Q0])});
            skCircle(sketch, "E89", {"center": v(0, 0) * mm, "radius": 11.5 * mm});
            skCircle(sketch, "E90", {"center": v(0, 0) * mm, "radius": 14 * mm});
            skCircle(sketch, "E91", {"center": v(0, 0) * mm, "radius": 12.75 * mm, "construction": true});
            skLineSegment(sketch, "E92", {"start": v(0, 0) * mm, "end": v(0, 14) * mm, "construction": true});
            skLineSegment(sketch, "E93", {"start": v(0, 0) * mm, "end": v(-1, 12.71) * mm, "construction": true});
            skLineSegment(sketch, "E94", {"start": v(0, 11.5) * mm, "end": v(15, 11.5) * mm, "construction": true});
            skArc(sketch, "E95", {"start": v(-0.85, 13.97) * mm, "mid": v(-1, 12.72) * mm, "end": v(-1.05, 11.45) * mm});
            skArc(sketch, "E96.0.MirrorCS", {"start": v(0.85, 13.97) * mm, "mid": v(1, 12.72) * mm, "end": v(1.05, 11.45) * mm});
            skArc(sketch, "E97.1.0", {"start": v(-5.13, 13.03) * mm, "mid": v(-4.88, 11.79) * mm, "end": v(-4.53, 10.57) * mm});
            skArc(sketch, "E97.1.1", {"start": v(-3.5, 13.55) * mm, "mid": v(-2.98, 12.4) * mm, "end": v(-2.54, 11.22) * mm});
            skArc(sketch, "E97.2.0", {"start": v(-8.9, 10.8) * mm, "mid": v(-8.28, 9.7) * mm, "end": v(-7.58, 8.65) * mm});
            skArc(sketch, "E97.2.1", {"start": v(-7.52, 11.8) * mm, "mid": v(-6.67, 10.88) * mm, "end": v(-5.89, 9.88) * mm});
            skArc(sketch, "E97.3.0", {"start": v(-11.8, 7.52) * mm, "mid": v(-10.88, 6.67) * mm, "end": v(-9.88, 5.89) * mm});
            skArc(sketch, "E97.3.1", {"start": v(-10.8, 8.9) * mm, "mid": v(-9.7, 8.28) * mm, "end": v(-8.65, 7.58) * mm});
            skArc(sketch, "E97.4.0", {"start": v(-13.55, 3.5) * mm, "mid": v(-12.4, 2.98) * mm, "end": v(-11.22, 2.54) * mm});
            skArc(sketch, "E97.4.1", {"start": v(-13.03, 5.13) * mm, "mid": v(-11.79, 4.88) * mm, "end": v(-10.57, 4.53) * mm});
            skArc(sketch, "E97.5.0", {"start": v(-13.97, -0.85) * mm, "mid": v(-12.72, -1) * mm, "end": v(-11.45, -1.05) * mm});
            skArc(sketch, "E97.5.1", {"start": v(-13.97, 0.85) * mm, "mid": v(-12.72, 1) * mm, "end": v(-11.45, 1.05) * mm});
            skArc(sketch, "E97.6.0", {"start": v(-13.03, -5.13) * mm, "mid": v(-11.79, -4.88) * mm, "end": v(-10.57, -4.53) * mm});
            skArc(sketch, "E97.6.1", {"start": v(-13.55, -3.5) * mm, "mid": v(-12.4, -2.98) * mm, "end": v(-11.22, -2.54) * mm});
            skArc(sketch, "E97.7.0", {"start": v(-10.8, -8.9) * mm, "mid": v(-9.7, -8.28) * mm, "end": v(-8.65, -7.58) * mm});
            skArc(sketch, "E97.7.1", {"start": v(-11.8, -7.52) * mm, "mid": v(-10.88, -6.67) * mm, "end": v(-9.88, -5.89) * mm});
            skArc(sketch, "E97.8.0", {"start": v(-7.52, -11.8) * mm, "mid": v(-6.67, -10.88) * mm, "end": v(-5.89, -9.88) * mm});
            skArc(sketch, "E97.8.1", {"start": v(-8.9, -10.8) * mm, "mid": v(-8.28, -9.7) * mm, "end": v(-7.58, -8.65) * mm});
            skArc(sketch, "E97.9.0", {"start": v(-3.5, -13.55) * mm, "mid": v(-2.98, -12.4) * mm, "end": v(-2.54, -11.22) * mm});
            skArc(sketch, "E97.9.1", {"start": v(-5.13, -13.03) * mm, "mid": v(-4.88, -11.79) * mm, "end": v(-4.53, -10.57) * mm});
            skArc(sketch, "E97.10.0", {"start": v(0.85, -13.97) * mm, "mid": v(1, -12.72) * mm, "end": v(1.05, -11.45) * mm});
            skArc(sketch, "E97.10.1", {"start": v(-0.85, -13.97) * mm, "mid": v(-1, -12.72) * mm, "end": v(-1.05, -11.45) * mm});
            skArc(sketch, "E97.11.0", {"start": v(5.13, -13.03) * mm, "mid": v(4.88, -11.79) * mm, "end": v(4.53, -10.57) * mm});
            skArc(sketch, "E97.11.1", {"start": v(3.5, -13.55) * mm, "mid": v(2.98, -12.4) * mm, "end": v(2.54, -11.22) * mm});
            skArc(sketch, "E97.12.0", {"start": v(8.9, -10.8) * mm, "mid": v(8.28, -9.7) * mm, "end": v(7.58, -8.65) * mm});
            skArc(sketch, "E97.12.1", {"start": v(7.52, -11.8) * mm, "mid": v(6.67, -10.88) * mm, "end": v(5.89, -9.88) * mm});
            skArc(sketch, "E97.13.0", {"start": v(11.8, -7.52) * mm, "mid": v(10.88, -6.67) * mm, "end": v(9.88, -5.89) * mm});
            skArc(sketch, "E97.13.1", {"start": v(10.8, -8.9) * mm, "mid": v(9.7, -8.28) * mm, "end": v(8.65, -7.58) * mm});
            skArc(sketch, "E97.14.0", {"start": v(13.55, -3.5) * mm, "mid": v(12.4, -2.98) * mm, "end": v(11.22, -2.54) * mm});
            skArc(sketch, "E97.14.1", {"start": v(13.03, -5.13) * mm, "mid": v(11.79, -4.88) * mm, "end": v(10.57, -4.53) * mm});
            skArc(sketch, "E97.15.0", {"start": v(13.97, 0.85) * mm, "mid": v(12.72, 1) * mm, "end": v(11.45, 1.05) * mm});
            skArc(sketch, "E97.15.1", {"start": v(13.97, -0.85) * mm, "mid": v(12.72, -1) * mm, "end": v(11.45, -1.05) * mm});
            skArc(sketch, "E97.16.0", {"start": v(13.03, 5.13) * mm, "mid": v(11.79, 4.88) * mm, "end": v(10.57, 4.53) * mm});
            skArc(sketch, "E97.16.1", {"start": v(13.55, 3.5) * mm, "mid": v(12.4, 2.98) * mm, "end": v(11.22, 2.54) * mm});
            skArc(sketch, "E97.17.0", {"start": v(10.8, 8.9) * mm, "mid": v(9.7, 8.28) * mm, "end": v(8.65, 7.58) * mm});
            skArc(sketch, "E97.17.1", {"start": v(11.8, 7.52) * mm, "mid": v(10.88, 6.67) * mm, "end": v(9.88, 5.89) * mm});
            skArc(sketch, "E97.18.0", {"start": v(7.52, 11.8) * mm, "mid": v(6.67, 10.88) * mm, "end": v(5.89, 9.88) * mm});
            skArc(sketch, "E97.18.1", {"start": v(8.9, 10.8) * mm, "mid": v(8.28, 9.7) * mm, "end": v(7.58, 8.65) * mm});
            skArc(sketch, "E97.19.0", {"start": v(3.5, 13.55) * mm, "mid": v(2.98, 12.4) * mm, "end": v(2.54, 11.22) * mm});
            skArc(sketch, "E97.19.1", {"start": v(5.13, 13.03) * mm, "mid": v(4.88, 11.79) * mm, "end": v(4.53, 10.57) * mm});
            skSolve(sketch);
        }
        {
            var Q0;
            Q0=makeQuery(id+"F44.imprint","IMPRINT",FACE,{"disambiguationData":[TD([[makeQuery(id+"F44.imprint","IMPRINT",EDGE,{"derivedFrom":makeQuery(id+"F29.opExtrude","CAP_EDGE",EDGE,{"disambiguationData":[OSD([sQuery(id+"F27.wireOp",EDGE,"E60")])],"isStart":true})}),-1.0]])]});
            var Q1;
            Q1=makeQuery(id+"F44.imprint","IMPRINT",FACE,{"disambiguationData":[TD([[makeQuery(id+"F44.imprint","IMPRINT",EDGE,{"derivedFrom":makeQuery(id+"F29.opExtrude","CAP_EDGE",EDGE,{"disambiguationData":[OSD([sQuery(id+"F27.wireOp",EDGE,"E60")])],"isStart":true})}),1.0]])]});
            var Q2;
            {var subQ1=sQuery(id+"F44.wireOp",EDGE,"E95");Q2=makeQuery(id+"F44.imprint","IMPRINT",FACE,{"disambiguationData":[TD([[makeQuery(id+"F44.imprint","IMPRINT",EDGE,{"derivedFrom":subQ1}),1.0]])]});}
            var Q3;
            {var subQ1=sQuery(id+"F44.wireOp",EDGE,"E97.19.0");Q3=makeQuery(id+"F44.imprint","IMPRINT",FACE,{"disambiguationData":[TD([[makeQuery(id+"F44.imprint","IMPRINT",EDGE,{"derivedFrom":subQ1}),1.0]])]});}
            var Q4;
            {var subQ1=sQuery(id+"F44.wireOp",EDGE,"E97.18.0");Q4=makeQuery(id+"F44.imprint","IMPRINT",FACE,{"disambiguationData":[TD([[makeQuery(id+"F44.imprint","IMPRINT",EDGE,{"derivedFrom":subQ1}),1.0]])]});}
            var Q5;
            {var subQ1=sQuery(id+"F44.wireOp",EDGE,"E97.17.0");Q5=makeQuery(id+"F44.imprint","IMPRINT",FACE,{"disambiguationData":[TD([[makeQuery(id+"F44.imprint","IMPRINT",EDGE,{"derivedFrom":subQ1}),1.0]])]});}
            var Q6;
            {var subQ1=sQuery(id+"F44.wireOp",EDGE,"E97.16.0");Q6=makeQuery(id+"F44.imprint","IMPRINT",FACE,{"disambiguationData":[TD([[makeQuery(id+"F44.imprint","IMPRINT",EDGE,{"derivedFrom":subQ1}),1.0]])]});}
            var Q7;
            {var subQ1=sQuery(id+"F44.wireOp",EDGE,"E97.15.0");Q7=makeQuery(id+"F44.imprint","IMPRINT",FACE,{"disambiguationData":[TD([[makeQuery(id+"F44.imprint","IMPRINT",EDGE,{"derivedFrom":subQ1}),1.0]])]});}
            var Q8;
            {var subQ1=sQuery(id+"F44.wireOp",EDGE,"E97.14.0");Q8=makeQuery(id+"F44.imprint","IMPRINT",FACE,{"disambiguationData":[TD([[makeQuery(id+"F44.imprint","IMPRINT",EDGE,{"derivedFrom":subQ1}),1.0]])]});}
            var Q9;
            {var subQ1=sQuery(id+"F44.wireOp",EDGE,"E97.13.0");Q9=makeQuery(id+"F44.imprint","IMPRINT",FACE,{"disambiguationData":[TD([[makeQuery(id+"F44.imprint","IMPRINT",EDGE,{"derivedFrom":subQ1}),1.0]])]});}
            var Q10;
            {var subQ1=sQuery(id+"F44.wireOp",EDGE,"E97.12.0");Q10=makeQuery(id+"F44.imprint","IMPRINT",FACE,{"disambiguationData":[TD([[makeQuery(id+"F44.imprint","IMPRINT",EDGE,{"derivedFrom":subQ1}),1.0]])]});}
            var Q11;
            {var subQ1=sQuery(id+"F44.wireOp",EDGE,"E97.11.0");Q11=makeQuery(id+"F44.imprint","IMPRINT",FACE,{"disambiguationData":[TD([[makeQuery(id+"F44.imprint","IMPRINT",EDGE,{"derivedFrom":subQ1}),1.0]])]});}
            var Q12;
            {var subQ1=sQuery(id+"F44.wireOp",EDGE,"E97.10.0");Q12=makeQuery(id+"F44.imprint","IMPRINT",FACE,{"disambiguationData":[TD([[makeQuery(id+"F44.imprint","IMPRINT",EDGE,{"derivedFrom":subQ1}),1.0]])]});}
            var Q13;
            {var subQ1=sQuery(id+"F44.wireOp",EDGE,"E97.9.0");Q13=makeQuery(id+"F44.imprint","IMPRINT",FACE,{"disambiguationData":[TD([[makeQuery(id+"F44.imprint","IMPRINT",EDGE,{"derivedFrom":subQ1}),1.0]])]});}
            var Q14;
            {var subQ1=sQuery(id+"F44.wireOp",EDGE,"E97.8.0");Q14=makeQuery(id+"F44.imprint","IMPRINT",FACE,{"disambiguationData":[TD([[makeQuery(id+"F44.imprint","IMPRINT",EDGE,{"derivedFrom":subQ1}),1.0]])]});}
            var Q15;
            {var subQ2=sQuery(id+"F44.wireOp",EDGE,"E97.7.0");Q15=makeQuery(id+"F44.imprint","IMPRINT",FACE,{"disambiguationData":[TD([[makeQuery(id+"F44.imprint","IMPRINT",EDGE,{"derivedFrom":subQ2}),1.0]])]});}
            var Q16;
            {var subQ1=sQuery(id+"F44.wireOp",EDGE,"E97.6.0");Q16=makeQuery(id+"F44.imprint","IMPRINT",FACE,{"disambiguationData":[TD([[makeQuery(id+"F44.imprint","IMPRINT",EDGE,{"derivedFrom":subQ1}),1.0]])]});}
            var Q17;
            {var subQ1=sQuery(id+"F44.wireOp",EDGE,"E97.5.0");Q17=makeQuery(id+"F44.imprint","IMPRINT",FACE,{"disambiguationData":[TD([[makeQuery(id+"F44.imprint","IMPRINT",EDGE,{"derivedFrom":subQ1}),1.0]])]});}
            var Q18;
            {var subQ1=sQuery(id+"F44.wireOp",EDGE,"E97.4.0");Q18=makeQuery(id+"F44.imprint","IMPRINT",FACE,{"disambiguationData":[TD([[makeQuery(id+"F44.imprint","IMPRINT",EDGE,{"derivedFrom":subQ1}),1.0]])]});}
            var Q19;
            {var subQ1=sQuery(id+"F44.wireOp",EDGE,"E97.3.0");Q19=makeQuery(id+"F44.imprint","IMPRINT",FACE,{"disambiguationData":[TD([[makeQuery(id+"F44.imprint","IMPRINT",EDGE,{"derivedFrom":subQ1}),1.0]])]});}
            var Q20;
            {var subQ1=sQuery(id+"F44.wireOp",EDGE,"E97.2.0");Q20=makeQuery(id+"F44.imprint","IMPRINT",FACE,{"disambiguationData":[TD([[makeQuery(id+"F44.imprint","IMPRINT",EDGE,{"derivedFrom":subQ1}),1.0]])]});}
            var Q21;
            {var subQ1=sQuery(id+"F44.wireOp",EDGE,"E97.1.0");Q21=makeQuery(id+"F44.imprint","IMPRINT",FACE,{"disambiguationData":[TD([[makeQuery(id+"F44.imprint","IMPRINT",EDGE,{"derivedFrom":subQ1}),1.0]])]});}
            extrude(context, id + "F45", {"entities" : qUnion([Q0, Q1, Q2, Q3, Q4, Q5, Q6, Q7, Q8, Q9, Q10, Q11, Q12, Q13, Q14, Q15, Q16, Q17, Q18, Q19, Q20, Q21]), "depth" : 4 * mm});
        }
        {
            var Q0;
            Q0=qCreatedBy(makeId("Front.planeOp"),FACE);
            var sketch = newSketch(context, id + "F46", { "sketchPlane" : qUnion([Q0])});
            skLineSegment(sketch, "E98.0", {"start": v(29.8, -11.5) * mm, "end": v(29.8, 11.5) * mm});
            skLineSegment(sketch, "E98.1", {"start": v(29.8, -12.75) * mm, "end": v(29.8, 12.75) * mm});
            skLineSegment(sketch, "E98.2", {"start": v(29.8, -14) * mm, "end": v(29.8, 14) * mm});
            skLineSegment(sketch, "E99.bottom", {"start": v(29.8, 14) * mm, "end": v(25.8, 14) * mm});
            skLineSegment(sketch, "E99.top", {"start": v(29.8, 11.5) * mm, "end": v(25.8, 11.5) * mm});
            skLineSegment(sketch, "E99.left", {"start": v(29.8, 14) * mm, "end": v(29.8, 11.5) * mm});
            skLineSegment(sketch, "E99.right", {"start": v(25.8, 14) * mm, "end": v(25.8, 11.5) * mm});
            skLineSegment(sketch, "E100", {"start": v(27.8, 14) * mm, "end": v(27.8, 11.5) * mm, "construction": true});
            skLineSegment(sketch, "E101", {"start": v(29.8, 11.5) * mm, "end": v(19.8, 11.5) * mm, "construction": true});
            skLineSegment(sketch, "E102", {"start": v(29.8, 0) * mm, "end": v(24.27, 0) * mm, "construction": true});
            skArc(sketch, "E103", {"start": v(29.8, 12.75) * mm, "mid": v(29.7, 13.38) * mm, "end": v(29.56, 14) * mm});
            skArc(sketch, "E104.0.MirrorCS", {"start": v(25.8, 12.75) * mm, "mid": v(25.9, 13.38) * mm, "end": v(26.04, 14) * mm});
            skSolve(sketch);
        }
        {
            var Q0;
            {var subQ0=sQuery(id+"F46.wireOp",EDGE,"E104.0.MirrorCS");Q0=makeQuery(id+"F46.imprint","IMPRINT",FACE,{"disambiguationData":[TD([[makeQuery(id+"F46.imprint","IMPRINT",EDGE,{"derivedFrom":subQ0}),1.0]])]});}
            var Q1;
            {var subQ0=sQuery(id+"F46.wireOp",EDGE,"E103");Q1=makeQuery(id+"F46.imprint","IMPRINT",FACE,{"disambiguationData":[TD([[makeQuery(id+"F46.imprint","IMPRINT",EDGE,{"derivedFrom":subQ0}),-1.0]])]});}
            var Q2;
            Q2=sQuery(id+"F46.wireOp",EDGE,"E102");
            revolve(context, id + "F47", {"operationType" : NewBodyOperationType.REMOVE, "entities" : qUnion([Q0, Q1]), "axis" : qUnion([Q2]), "revolveType" : RevolveType.FULL, "oppositeDirection" : true});
        }
    });
